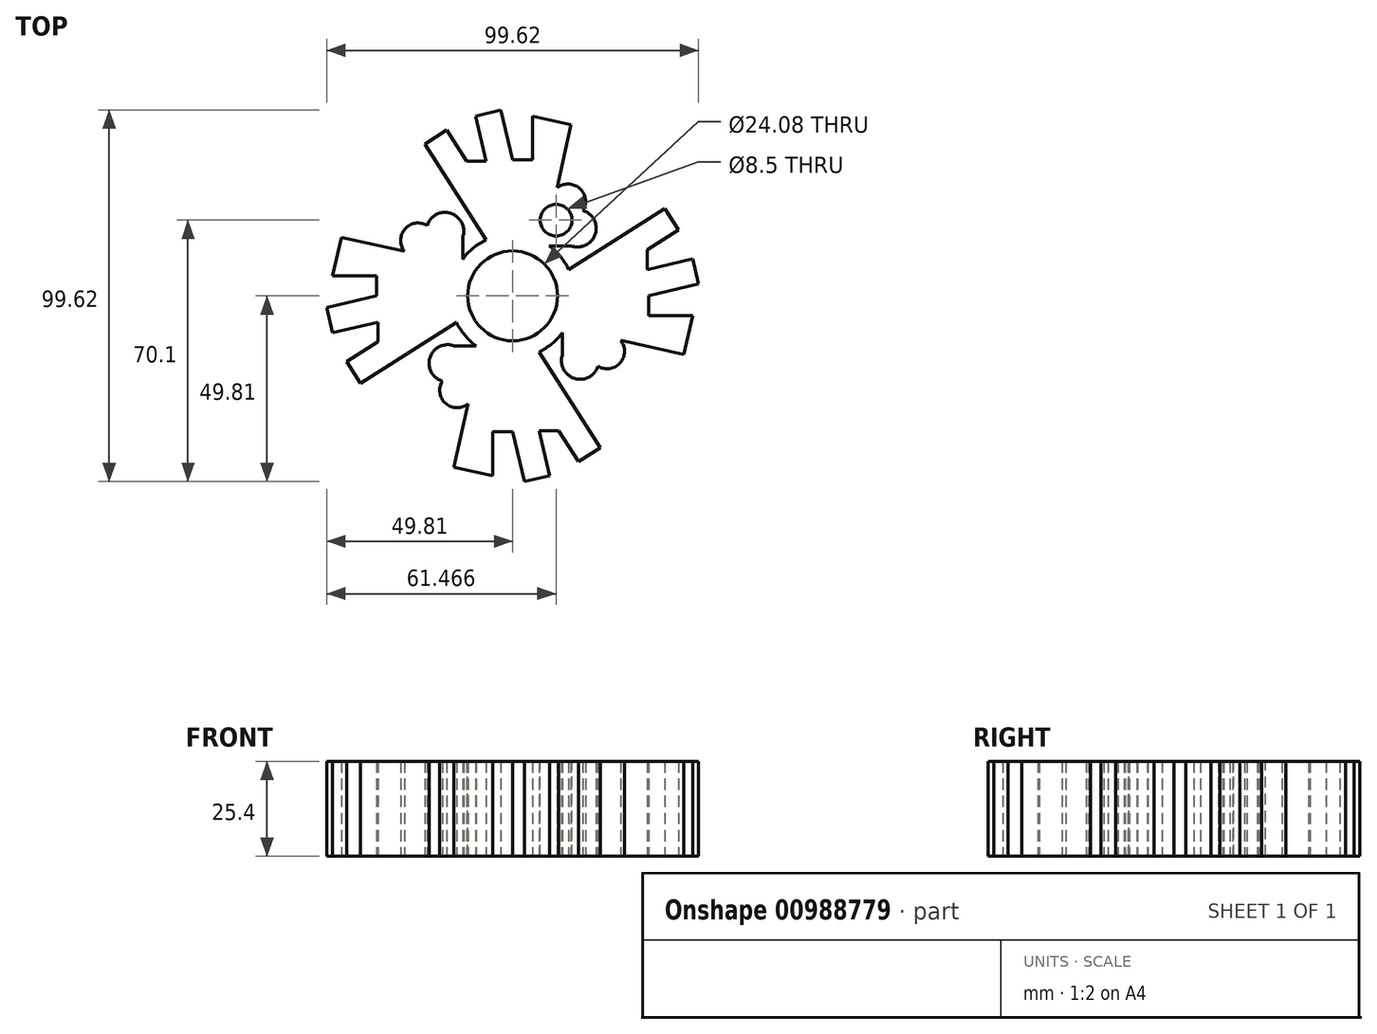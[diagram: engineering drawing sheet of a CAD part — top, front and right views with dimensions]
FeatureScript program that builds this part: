
annotation { "Feature Type Name" : "Feature", "Feature Type Description" : "" }
export const myFeature = defineFeature(function(context is Context, id is Id, definition is map)
    precondition{}
    {
        {
            var Q0;
            Q0=qCreatedBy(makeId("Top.planeOp"),FACE);
            var sketch = newSketch(context, id + "F0", { "sketchPlane" : qUnion([Q0])});
            skCircle(sketch, "E0", {"center": v(0, 0) * mm, "radius": 16.6 * mm});
            skLineSegment(sketch, "E1", {"start": v(-7.06, 15.02) * mm, "end": v(-23.46, 40.72) * mm});
            skLineSegment(sketch, "E2", {"start": v(-23.46, 40.72) * mm, "end": v(-17.65, 44.43) * mm});
            skLineSegment(sketch, "E3", {"start": v(-17.65, 44.43) * mm, "end": v(-12.34, 36.1) * mm});
            skLineSegment(sketch, "E4", {"start": v(-12.34, 36.1) * mm, "end": v(-7.05, 36.1) * mm});
            skLineSegment(sketch, "E5", {"start": v(-7.05, 36.1) * mm, "end": v(-9.93, 48.2) * mm});
            skLineSegment(sketch, "E6", {"start": v(-9.93, 48.2) * mm, "end": v(-3.18, 49.81) * mm});
            skLineSegment(sketch, "E7", {"start": v(-3.18, 49.81) * mm, "end": v(0, 36.42) * mm});
            skLineSegment(sketch, "E8", {"start": v(0, 36.42) * mm, "end": v(5.32, 36.42) * mm});
            skLineSegment(sketch, "E9", {"start": v(5.32, 36.42) * mm, "end": v(5.32, 48.2) * mm});
            skLineSegment(sketch, "E10", {"start": v(5.32, 48.2) * mm, "end": v(15.69, 45.9) * mm});
            skLineSegment(sketch, "E11", {"start": v(15.69, 45.9) * mm, "end": v(11.91, 28.93) * mm});
            skArc(sketch, "E12", {"start": v(18.85, 22.88) * mm, "mid": v(17.94, 28.83) * mm, "end": v(11.91, 28.93) * mm});
            skArc(sketch, "E13", {"start": v(15.69, 13.38) * mm, "mid": v(22.13, 16.51) * mm, "end": v(18.85, 22.88) * mm});
            skLineSegment(sketch, "E14", {"start": v(15.69, 13.38) * mm, "end": v(9.82, 13.38) * mm});
            skLineSegment(sketch, "E15.1.0", {"start": v(-44.43, -17.65) * mm, "end": v(-36.1, -12.34) * mm});
            skLineSegment(sketch, "E15.1.1", {"start": v(-15.02, -7.06) * mm, "end": v(-40.72, -23.46) * mm});
            skArc(sketch, "E15.1.2", {"start": v(-22.88, 18.85) * mm, "mid": v(-28.83, 17.94) * mm, "end": v(-28.93, 11.91) * mm});
            skLineSegment(sketch, "E15.1.3", {"start": v(-36.42, 5.32) * mm, "end": v(-48.2, 5.32) * mm});
            skLineSegment(sketch, "E15.1.4", {"start": v(-45.9, 15.69) * mm, "end": v(-28.93, 11.91) * mm});
            skLineSegment(sketch, "E15.1.5", {"start": v(-36.1, -7.05) * mm, "end": v(-48.2, -9.93) * mm});
            skLineSegment(sketch, "E15.1.6", {"start": v(-48.2, 5.32) * mm, "end": v(-45.9, 15.69) * mm});
            skLineSegment(sketch, "E15.1.7", {"start": v(-49.81, -3.18) * mm, "end": v(-36.42, 0) * mm});
            skLineSegment(sketch, "E15.1.8", {"start": v(-48.2, -9.93) * mm, "end": v(-49.81, -3.18) * mm});
            skLineSegment(sketch, "E15.1.9", {"start": v(-40.72, -23.46) * mm, "end": v(-44.43, -17.65) * mm});
            skLineSegment(sketch, "E15.1.10", {"start": v(-36.42, 0) * mm, "end": v(-36.42, 5.32) * mm});
            skLineSegment(sketch, "E15.1.11", {"start": v(-36.1, -12.34) * mm, "end": v(-36.1, -7.05) * mm});
            skArc(sketch, "E15.1.12", {"start": v(-13.38, 15.69) * mm, "mid": v(-16.51, 22.13) * mm, "end": v(-22.88, 18.85) * mm});
            skLineSegment(sketch, "E15.1.13", {"start": v(-13.38, 15.69) * mm, "end": v(-13.38, 9.82) * mm});
            skLineSegment(sketch, "E15.2.0", {"start": v(17.65, -44.43) * mm, "end": v(12.34, -36.1) * mm});
            skLineSegment(sketch, "E15.2.1", {"start": v(7.06, -15.02) * mm, "end": v(23.46, -40.72) * mm});
            skArc(sketch, "E15.2.2", {"start": v(-18.85, -22.88) * mm, "mid": v(-17.94, -28.83) * mm, "end": v(-11.91, -28.93) * mm});
            skLineSegment(sketch, "E15.2.3", {"start": v(-5.32, -36.42) * mm, "end": v(-5.32, -48.2) * mm});
            skLineSegment(sketch, "E15.2.4", {"start": v(-15.69, -45.9) * mm, "end": v(-11.91, -28.93) * mm});
            skLineSegment(sketch, "E15.2.5", {"start": v(7.05, -36.1) * mm, "end": v(9.93, -48.2) * mm});
            skLineSegment(sketch, "E15.2.6", {"start": v(-5.32, -48.2) * mm, "end": v(-15.69, -45.9) * mm});
            skLineSegment(sketch, "E15.2.7", {"start": v(3.18, -49.81) * mm, "end": v(0, -36.42) * mm});
            skLineSegment(sketch, "E15.2.8", {"start": v(9.93, -48.2) * mm, "end": v(3.18, -49.81) * mm});
            skLineSegment(sketch, "E15.2.9", {"start": v(23.46, -40.72) * mm, "end": v(17.65, -44.43) * mm});
            skLineSegment(sketch, "E15.2.10", {"start": v(0, -36.42) * mm, "end": v(-5.32, -36.42) * mm});
            skLineSegment(sketch, "E15.2.11", {"start": v(12.34, -36.1) * mm, "end": v(7.05, -36.1) * mm});
            skArc(sketch, "E15.2.12", {"start": v(-15.69, -13.38) * mm, "mid": v(-22.13, -16.51) * mm, "end": v(-18.85, -22.88) * mm});
            skLineSegment(sketch, "E15.2.13", {"start": v(-15.69, -13.38) * mm, "end": v(-9.82, -13.38) * mm});
            skLineSegment(sketch, "E15.3.0", {"start": v(44.43, 17.65) * mm, "end": v(36.1, 12.34) * mm});
            skLineSegment(sketch, "E15.3.1", {"start": v(15.02, 7.06) * mm, "end": v(40.72, 23.46) * mm});
            skArc(sketch, "E15.3.2", {"start": v(22.88, -18.85) * mm, "mid": v(28.83, -17.94) * mm, "end": v(28.93, -11.91) * mm});
            skLineSegment(sketch, "E15.3.3", {"start": v(36.42, -5.32) * mm, "end": v(48.2, -5.32) * mm});
            skLineSegment(sketch, "E15.3.4", {"start": v(45.9, -15.69) * mm, "end": v(28.93, -11.91) * mm});
            skLineSegment(sketch, "E15.3.5", {"start": v(36.1, 7.05) * mm, "end": v(48.2, 9.93) * mm});
            skLineSegment(sketch, "E15.3.6", {"start": v(48.2, -5.32) * mm, "end": v(45.9, -15.69) * mm});
            skLineSegment(sketch, "E15.3.7", {"start": v(49.81, 3.18) * mm, "end": v(36.42, 0) * mm});
            skLineSegment(sketch, "E15.3.8", {"start": v(48.2, 9.93) * mm, "end": v(49.81, 3.18) * mm});
            skLineSegment(sketch, "E15.3.9", {"start": v(40.72, 23.46) * mm, "end": v(44.43, 17.65) * mm});
            skLineSegment(sketch, "E15.3.10", {"start": v(36.42, 0) * mm, "end": v(36.42, -5.32) * mm});
            skLineSegment(sketch, "E15.3.11", {"start": v(36.1, 12.34) * mm, "end": v(36.1, 7.05) * mm});
            skArc(sketch, "E15.3.12", {"start": v(13.38, -15.69) * mm, "mid": v(16.51, -22.13) * mm, "end": v(22.88, -18.85) * mm});
            skLineSegment(sketch, "E15.3.13", {"start": v(13.38, -15.69) * mm, "end": v(13.38, -9.82) * mm});
            skSolve(sketch);
        }
        {
            var Q0;
            Q0=makeQuery(id+"F0.imprint","IMPRINT",FACE,{"disambiguationData":[TD([[makeQuery(id+"F0.imprint","IMPRINT",EDGE,{"derivedFrom":sQuery(id+"F0.wireOp",EDGE,"E15.1.0")}),-1.0]])]});
            var Q1;
            {var subQ0=sQuery(id+"F0.wireOp",EDGE,"E0");var subQ4=makeQuery(id+"F0.imprint","INTERSECT",VERTEX,{"derivedFrom":[subQ0,sQuery(id+"F0.wireOp",EDGE,"E14")]});Q1=makeQuery(id+"F0.imprint","IMPRINT",FACE,{"disambiguationData":[TD([[makeQuery(id+"F0.imprint","IMPRINT",EDGE,{"disambiguationData":[TD([[subQ4,1.0]])],"derivedFrom":subQ0}),1.0]])]});}
            var Q2;
            Q2=makeQuery(id+"F0.imprint","IMPRINT",FACE,{"disambiguationData":[TD([[makeQuery(id+"F0.imprint","IMPRINT",EDGE,{"derivedFrom":sQuery(id+"F0.wireOp",EDGE,"E15.3.0")}),-1.0]])]});
            var Q3;
            Q3=makeQuery(id+"F0.imprint","IMPRINT",FACE,{"disambiguationData":[TD([[makeQuery(id+"F0.imprint","IMPRINT",EDGE,{"derivedFrom":sQuery(id+"F0.wireOp",EDGE,"E15.2.0")}),-1.0]])]});
            var Q4;
            {var subQ0=sQuery(id+"F0.wireOp",EDGE,"E1");Q4=makeQuery(id+"F0.imprint","IMPRINT",FACE,{"disambiguationData":[TD([[makeQuery(id+"F0.imprint","IMPRINT",EDGE,{"derivedFrom":subQ0}),-1.0]])]});}
            extrude(context, id + "F1", {"entities" : qUnion([Q0, Q1, Q2, Q3, Q4]), "depth" : 25.4 * mm, "offsetDistance" : 25.4 * mm});
        }
        {
            var Q0;
            Q0=makeQuery(id+"F1.opExtrude","CAP_FACE",FACE,{"disambiguationData":[OSD([sQuery(id+"F0.wireOp",EDGE,"E0"),sQuery(id+"F0.wireOp",EDGE,"E1"),sQuery(id+"F0.wireOp",EDGE,"E2"),sQuery(id+"F0.wireOp",EDGE,"E3"),sQuery(id+"F0.wireOp",EDGE,"E4"),sQuery(id+"F0.wireOp",EDGE,"E5"),sQuery(id+"F0.wireOp",EDGE,"E6"),sQuery(id+"F0.wireOp",EDGE,"E7"),sQuery(id+"F0.wireOp",EDGE,"E8"),sQuery(id+"F0.wireOp",EDGE,"E9"),sQuery(id+"F0.wireOp",EDGE,"E10"),sQuery(id+"F0.wireOp",EDGE,"E11"),sQuery(id+"F0.wireOp",EDGE,"E12"),sQuery(id+"F0.wireOp",EDGE,"E13"),sQuery(id+"F0.wireOp",EDGE,"E14"),sQuery(id+"F0.wireOp",EDGE,"E15.1.0"),sQuery(id+"F0.wireOp",EDGE,"E15.1.1"),sQuery(id+"F0.wireOp",EDGE,"E15.1.2"),sQuery(id+"F0.wireOp",EDGE,"E15.1.3"),sQuery(id+"F0.wireOp",EDGE,"E15.1.4"),sQuery(id+"F0.wireOp",EDGE,"E15.1.5"),sQuery(id+"F0.wireOp",EDGE,"E15.1.6"),sQuery(id+"F0.wireOp",EDGE,"E15.1.7"),sQuery(id+"F0.wireOp",EDGE,"E15.1.8"),sQuery(id+"F0.wireOp",EDGE,"E15.1.9"),sQuery(id+"F0.wireOp",EDGE,"E15.1.10"),sQuery(id+"F0.wireOp",EDGE,"E15.1.11"),sQuery(id+"F0.wireOp",EDGE,"E15.1.12"),sQuery(id+"F0.wireOp",EDGE,"E15.1.13"),sQuery(id+"F0.wireOp",EDGE,"E15.2.0"),sQuery(id+"F0.wireOp",EDGE,"E15.2.1"),sQuery(id+"F0.wireOp",EDGE,"E15.2.2"),sQuery(id+"F0.wireOp",EDGE,"E15.2.3"),sQuery(id+"F0.wireOp",EDGE,"E15.2.4"),sQuery(id+"F0.wireOp",EDGE,"E15.2.5"),sQuery(id+"F0.wireOp",EDGE,"E15.2.6"),sQuery(id+"F0.wireOp",EDGE,"E15.2.7"),sQuery(id+"F0.wireOp",EDGE,"E15.2.8"),sQuery(id+"F0.wireOp",EDGE,"E15.2.9"),sQuery(id+"F0.wireOp",EDGE,"E15.2.10"),sQuery(id+"F0.wireOp",EDGE,"E15.2.11"),sQuery(id+"F0.wireOp",EDGE,"E15.2.12"),sQuery(id+"F0.wireOp",EDGE,"E15.2.13"),sQuery(id+"F0.wireOp",EDGE,"E15.3.0"),sQuery(id+"F0.wireOp",EDGE,"E15.3.1"),sQuery(id+"F0.wireOp",EDGE,"E15.3.2"),sQuery(id+"F0.wireOp",EDGE,"E15.3.3"),sQuery(id+"F0.wireOp",EDGE,"E15.3.4"),sQuery(id+"F0.wireOp",EDGE,"E15.3.5"),sQuery(id+"F0.wireOp",EDGE,"E15.3.6"),sQuery(id+"F0.wireOp",EDGE,"E15.3.7"),sQuery(id+"F0.wireOp",EDGE,"E15.3.8"),sQuery(id+"F0.wireOp",EDGE,"E15.3.9"),sQuery(id+"F0.wireOp",EDGE,"E15.3.10"),sQuery(id+"F0.wireOp",EDGE,"E15.3.11"),sQuery(id+"F0.wireOp",EDGE,"E15.3.12"),sQuery(id+"F0.wireOp",EDGE,"E15.3.13")])],"isStart":false});
            var sketch = newSketch(context, id + "F2", { "sketchPlane" : qUnion([Q0])});
            skCircle(sketch, "E16", {"center": v(0, 0) * mm, "radius": 12.04 * mm});
            skSolve(sketch);
        }
        {
            var Q0;
            Q0 = qSketchRegion(id + "F2", true);
            extrude(context, id + "F3", {"entities" : qUnion([Q0]), "operationType" : NewBodyOperationType.REMOVE, "oppositeDirection" : true, "depth" : 25.4 * mm, "offsetDistance" : 25.4 * mm});
        }
        {
            var Q0;
            Q0=makeQuery(id+"F1.opExtrude","CAP_FACE",FACE,{"disambiguationData":[OSD([sQuery(id+"F0.wireOp",EDGE,"E0"),sQuery(id+"F0.wireOp",EDGE,"E1"),sQuery(id+"F0.wireOp",EDGE,"E2"),sQuery(id+"F0.wireOp",EDGE,"E3"),sQuery(id+"F0.wireOp",EDGE,"E4"),sQuery(id+"F0.wireOp",EDGE,"E5"),sQuery(id+"F0.wireOp",EDGE,"E6"),sQuery(id+"F0.wireOp",EDGE,"E7"),sQuery(id+"F0.wireOp",EDGE,"E8"),sQuery(id+"F0.wireOp",EDGE,"E9"),sQuery(id+"F0.wireOp",EDGE,"E10"),sQuery(id+"F0.wireOp",EDGE,"E11"),sQuery(id+"F0.wireOp",EDGE,"E12"),sQuery(id+"F0.wireOp",EDGE,"E13"),sQuery(id+"F0.wireOp",EDGE,"E14"),sQuery(id+"F0.wireOp",EDGE,"E15.1.0"),sQuery(id+"F0.wireOp",EDGE,"E15.1.1"),sQuery(id+"F0.wireOp",EDGE,"E15.1.2"),sQuery(id+"F0.wireOp",EDGE,"E15.1.3"),sQuery(id+"F0.wireOp",EDGE,"E15.1.4"),sQuery(id+"F0.wireOp",EDGE,"E15.1.5"),sQuery(id+"F0.wireOp",EDGE,"E15.1.6"),sQuery(id+"F0.wireOp",EDGE,"E15.1.7"),sQuery(id+"F0.wireOp",EDGE,"E15.1.8"),sQuery(id+"F0.wireOp",EDGE,"E15.1.9"),sQuery(id+"F0.wireOp",EDGE,"E15.1.10"),sQuery(id+"F0.wireOp",EDGE,"E15.1.11"),sQuery(id+"F0.wireOp",EDGE,"E15.1.12"),sQuery(id+"F0.wireOp",EDGE,"E15.1.13"),sQuery(id+"F0.wireOp",EDGE,"E15.2.0"),sQuery(id+"F0.wireOp",EDGE,"E15.2.1"),sQuery(id+"F0.wireOp",EDGE,"E15.2.2"),sQuery(id+"F0.wireOp",EDGE,"E15.2.3"),sQuery(id+"F0.wireOp",EDGE,"E15.2.4"),sQuery(id+"F0.wireOp",EDGE,"E15.2.5"),sQuery(id+"F0.wireOp",EDGE,"E15.2.6"),sQuery(id+"F0.wireOp",EDGE,"E15.2.7"),sQuery(id+"F0.wireOp",EDGE,"E15.2.8"),sQuery(id+"F0.wireOp",EDGE,"E15.2.9"),sQuery(id+"F0.wireOp",EDGE,"E15.2.10"),sQuery(id+"F0.wireOp",EDGE,"E15.2.11"),sQuery(id+"F0.wireOp",EDGE,"E15.2.12"),sQuery(id+"F0.wireOp",EDGE,"E15.2.13"),sQuery(id+"F0.wireOp",EDGE,"E15.3.0"),sQuery(id+"F0.wireOp",EDGE,"E15.3.1"),sQuery(id+"F0.wireOp",EDGE,"E15.3.2"),sQuery(id+"F0.wireOp",EDGE,"E15.3.3"),sQuery(id+"F0.wireOp",EDGE,"E15.3.4"),sQuery(id+"F0.wireOp",EDGE,"E15.3.5"),sQuery(id+"F0.wireOp",EDGE,"E15.3.6"),sQuery(id+"F0.wireOp",EDGE,"E15.3.7"),sQuery(id+"F0.wireOp",EDGE,"E15.3.8"),sQuery(id+"F0.wireOp",EDGE,"E15.3.9"),sQuery(id+"F0.wireOp",EDGE,"E15.3.10"),sQuery(id+"F0.wireOp",EDGE,"E15.3.11"),sQuery(id+"F0.wireOp",EDGE,"E15.3.12"),sQuery(id+"F0.wireOp",EDGE,"E15.3.13")])],"isStart":false});
            var sketch = newSketch(context, id + "F4", { "sketchPlane" : qUnion([Q0])});
            skCircle(sketch, "E17", {"center": v(11.66, 20.3) * mm, "radius": 4.25 * mm});
            skSolve(sketch);
        }
        {
            var Q0;
            Q0=makeQuery(id+"F4.imprint","IMPRINT",FACE,{"disambiguationData":[TD([[makeQuery(id+"F4.imprint","IMPRINT",EDGE,{"derivedFrom":sQuery(id+"F4.wireOp",EDGE,"E17")}),1.0]])]});
            extrude(context, id + "F5", {"entities" : qUnion([Q0]), "operationType" : NewBodyOperationType.REMOVE, "endBound" : BoundingType.THROUGH_ALL, "oppositeDirection" : true, "depth" : 25.4 * mm, "offsetDistance" : 25.4 * mm});
        }
    });
